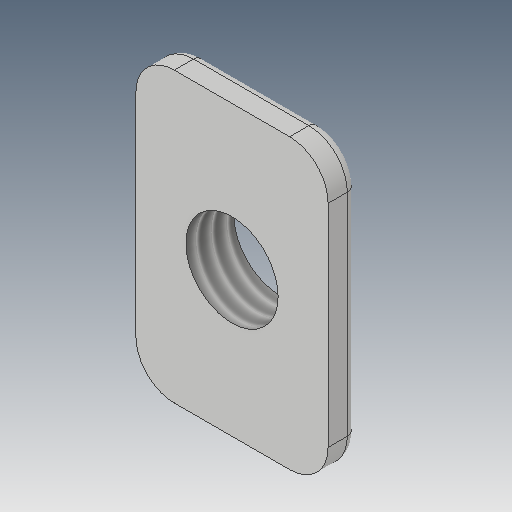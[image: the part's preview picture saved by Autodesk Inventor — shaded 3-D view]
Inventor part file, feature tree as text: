
AUTODESK INVENTOR PART (.ipt)
format: ipt  version: 2017 (Build 210142000, 142)  size: 159,744 bytes
history: native  units: mm
features: other x3, sketch x2
ambient origin geometry x8: Origin, YZ Plane, XZ Plane, XY Plane, X Axis, Y Axis, Z Axis, Center Point
bodies: Solid1 (feature_tree)
feature tree (5):
  other  "M5 Tee Nut-Generic_MIR_CPY_MIR.ipt"
  other  "Solid1::M5 Tee Nut-Generic_MIR_CPY_MIR.ipt"
  other  "TaggingFeature1"
  sketch  "Sketch1"  dims[d0=10.0mm]
  sketch  "Sketch2"
